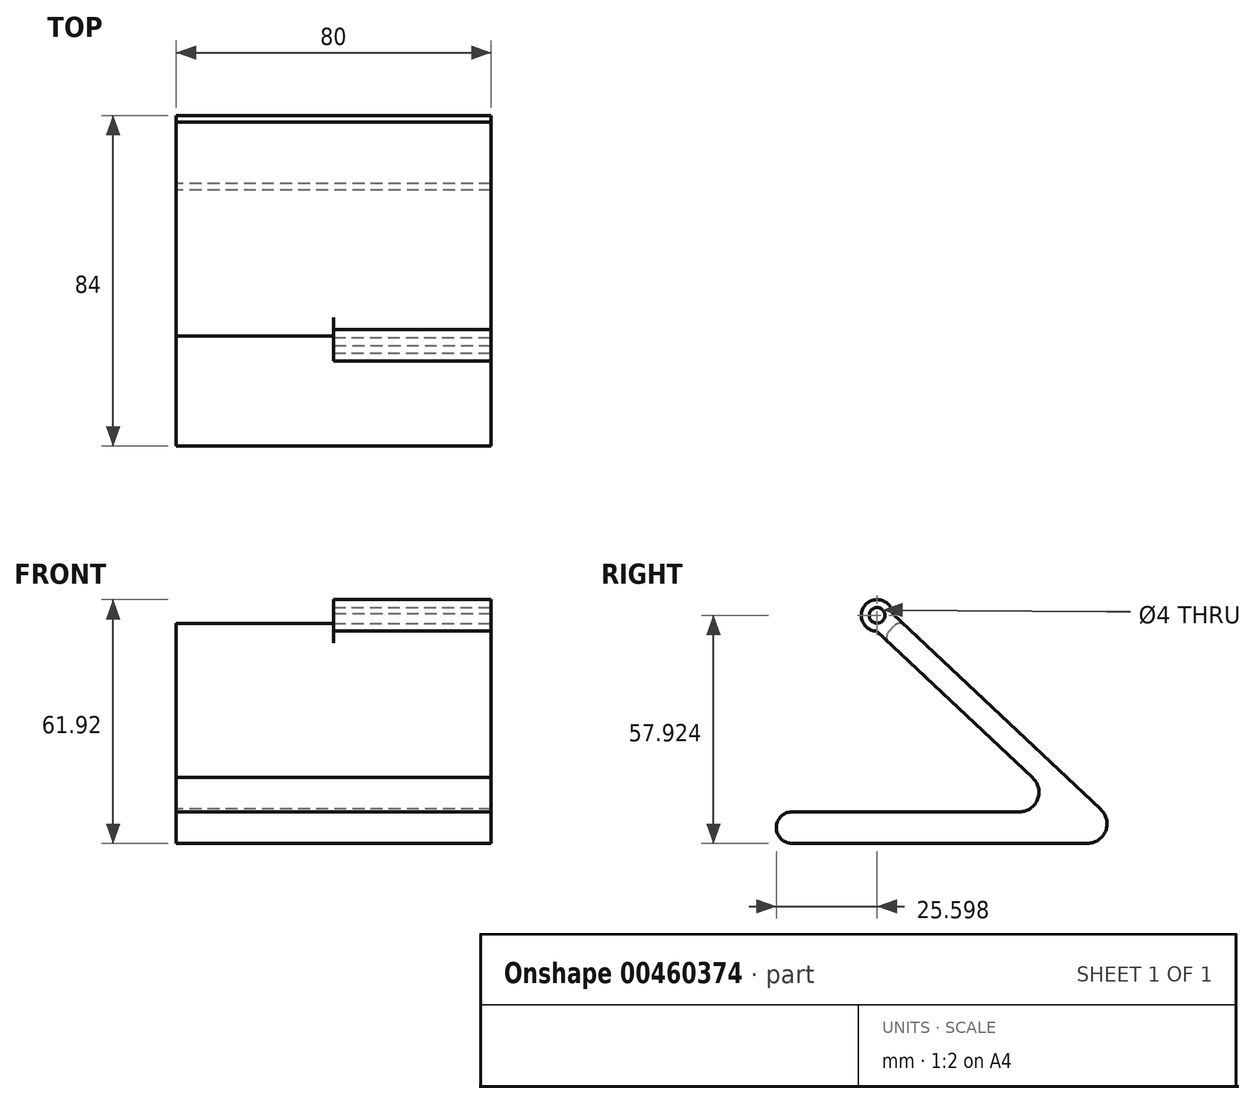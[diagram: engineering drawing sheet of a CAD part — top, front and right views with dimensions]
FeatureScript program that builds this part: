
annotation { "Feature Type Name" : "Feature", "Feature Type Description" : "" }
export const myFeature = defineFeature(function(context is Context, id is Id, definition is map)
    precondition{}
    {
        {
            var Q0;
            Q0=qCreatedBy(makeId("Right.planeOp"),FACE);
            var sketch = newSketch(context, id + "F0", { "sketchPlane" : qUnion([Q0])});
            skLineSegment(sketch, "E0", {"start": v(-63.48, -15.33) * mm, "end": v(11.52, -15.33) * mm});
            skLineSegment(sketch, "E1", {"start": v(-5.76, -7.33) * mm, "end": v(-63.48, -7.33) * mm});
            skPoint(sketch, "E2.visualSharp", {"position": v(7.24, -7.33) * mm});
            skArc(sketch, "E2.filletArc", {"start": v(-5.76, -7.33) * mm, "mid": v(-1.09, -4.13) * mm, "end": v(-2.4, 1.37) * mm});
            skPoint(sketch, "E3.visualSharp", {"position": v(24.5, -15.33) * mm});
            skArc(sketch, "E3.filletArc", {"start": v(11.52, -15.33) * mm, "mid": v(16.18, -12.13) * mm, "end": v(14.87, -6.63) * mm});
            skArc(sketch, "E4", {"start": v(-63.48, -7.33) * mm, "mid": v(-67.48, -11.33) * mm, "end": v(-63.48, -15.33) * mm});
            skLineSegment(sketch, "E5", {"start": v(-40.25, 36.94) * mm, "end": v(-36.23, 41.4) * mm});
            skLineSegment(sketch, "E6", {"start": v(-40.25, 36.94) * mm, "end": v(-2.4, 1.37) * mm});
            skLineSegment(sketch, "E7", {"start": v(-36.23, 41.4) * mm, "end": v(14.87, -6.63) * mm});
            skSolve(sketch);
        }
        {
            var Q0;
            Q0=makeQuery(id+"F0.imprint","IMPRINT",FACE,{"disambiguationData":[TD([[makeQuery(id+"F0.imprint","IMPRINT",EDGE,{"derivedFrom":sQuery(id+"F0.wireOp",EDGE,"E0")}),1.0]])]});
            extrude(context, id + "F1", {"entities" : qUnion([Q0]), "depth" : 40 * mm});
        }
        {
            var Q0;
            Q0=qCreatedBy(makeId("Right.planeOp"),FACE);
            cPlane(context, id + "F2", {"entities" : qUnion([Q0]), "cplaneType" : CPlaneType.OFFSET, "offset" : 40 * mm, "width" : 150 * mm, "height" : 150 * mm});
        }
        {
            var Q0;
            Q0=qCreatedBy(id+"F2.planeOp",FACE);
            var sketch = newSketch(context, id + "F3", { "sketchPlane" : qUnion([Q0])});
            skLineSegment(sketch, "E8.0.0", {"start": v(-36.23, 41.4) * mm, "end": v(-40.25, 36.94) * mm});
            skLineSegment(sketch, "E8.0.1", {"start": v(-40.25, 36.94) * mm, "end": v(-2.4, 1.37) * mm});
            skArc(sketch, "E8.0.2", {"start": v(-2.4, 1.37) * mm, "mid": v(-1.09, -4.13) * mm, "end": v(-5.76, -7.33) * mm});
            skLineSegment(sketch, "E8.0.3", {"start": v(-5.76, -7.33) * mm, "end": v(-63.48, -7.33) * mm});
            skArc(sketch, "E8.0.4", {"start": v(-63.48, -7.33) * mm, "mid": v(-67.48, -11.33) * mm, "end": v(-63.48, -15.33) * mm});
            skLineSegment(sketch, "E8.0.5", {"start": v(-63.48, -15.33) * mm, "end": v(11.52, -15.33) * mm});
            skArc(sketch, "E8.0.6", {"start": v(11.52, -15.33) * mm, "mid": v(16.18, -12.13) * mm, "end": v(14.87, -6.63) * mm});
            skLineSegment(sketch, "E8.0.7", {"start": v(14.87, -6.63) * mm, "end": v(-36.23, 41.4) * mm});
            skLineSegment(sketch, "E9", {"start": v(-40.25, 36.94) * mm, "end": v(-51.72, 47.72) * mm, "construction": true});
            skLineSegment(sketch, "E10", {"start": v(-36.23, 41.4) * mm, "end": v(-47.07, 51.59) * mm, "construction": true});
            skCircle(sketch, "E11", {"center": v(-41.88, 42.6) * mm, "radius": 4 * mm});
            skLineSegment(sketch, "E12", {"start": v(-42, 38.6) * mm, "end": v(-40.25, 36.94) * mm});
            skLineSegment(sketch, "E13", {"start": v(-37.9, 42.97) * mm, "end": v(-36.23, 41.4) * mm});
            skSolve(sketch);
        }
        {
            var Q0;
            Q0 = qSketchRegion(id + "F3", true);
            extrude(context, id + "F4", {"entities" : qUnion([Q0]), "operationType" : NewBodyOperationType.ADD, "depth" : 40 * mm});
        }
        {
            var Q0;
            Q0=qCreatedBy(id+"F2.planeOp",FACE);
            cPlane(context, id + "F5", {"entities" : qUnion([Q0]), "cplaneType" : CPlaneType.OFFSET, "offset" : 80 * mm, "width" : 150 * mm, "height" : 150 * mm});
        }
        {
            var Q0;
            Q0=qCreatedBy(id+"F5.planeOp",FACE);
            var sketch = newSketch(context, id + "F6", { "sketchPlane" : qUnion([Q0])});
            skLineSegment(sketch, "E14.0", {"start": v(-36.23, 41.4) * mm, "end": v(-40.25, 36.94) * mm});
            skLineSegment(sketch, "E14.1", {"start": v(-40.25, 36.94) * mm, "end": v(-2.4, 1.37) * mm});
            skArc(sketch, "E14.2", {"start": v(-2.4, 1.37) * mm, "mid": v(-1.09, -4.13) * mm, "end": v(-5.76, -7.33) * mm});
            skLineSegment(sketch, "E14.3", {"start": v(-5.76, -7.33) * mm, "end": v(-63.48, -7.33) * mm});
            skArc(sketch, "E14.4", {"start": v(-63.48, -7.33) * mm, "mid": v(-67.48, -11.33) * mm, "end": v(-63.48, -15.33) * mm});
            skLineSegment(sketch, "E14.5", {"start": v(-63.48, -15.33) * mm, "end": v(11.52, -15.33) * mm});
            skArc(sketch, "E14.6", {"start": v(11.52, -15.33) * mm, "mid": v(16.18, -12.13) * mm, "end": v(14.87, -6.63) * mm});
            skLineSegment(sketch, "E14.7", {"start": v(14.87, -6.63) * mm, "end": v(-36.23, 41.4) * mm});
            skLineSegment(sketch, "E14.8", {"start": v(-40.25, 36.94) * mm, "end": v(-51.72, 47.72) * mm});
            skLineSegment(sketch, "E14.9", {"start": v(-36.23, 41.4) * mm, "end": v(-47.07, 51.59) * mm});
            skCircle(sketch, "E14.10", {"center": v(-41.88, 42.6) * mm, "radius": 4 * mm});
            skLineSegment(sketch, "E14.11", {"start": v(-42, 38.6) * mm, "end": v(-40.25, 36.94) * mm});
            skLineSegment(sketch, "E14.12", {"start": v(-37.9, 42.97) * mm, "end": v(-36.23, 41.4) * mm});
            skPoint(sketch, "E14.13", {"position": v(-41.88, 42.6) * mm});
            skPoint(sketch, "E14.14", {"position": v(-41.88, 42.6) * mm});
            skArc(sketch, "E14.15.0", {"start": v(11.52, -15.33) * mm, "mid": v(16.18, -12.13) * mm, "end": v(14.87, -6.63) * mm});
            skLineSegment(sketch, "E14.15.1", {"start": v(14.87, -6.63) * mm, "end": v(-37.9, 42.97) * mm});
            skArc(sketch, "E14.15.2", {"start": v(-37.9, 42.97) * mm, "mid": v(-44.8, 45.33) * mm, "end": v(-42, 38.6) * mm});
            skLineSegment(sketch, "E14.15.3", {"start": v(-42, 38.6) * mm, "end": v(-2.4, 1.37) * mm});
            skArc(sketch, "E14.15.4", {"start": v(-2.4, 1.37) * mm, "mid": v(-1.09, -4.13) * mm, "end": v(-5.76, -7.33) * mm});
            skLineSegment(sketch, "E14.15.5", {"start": v(-5.76, -7.33) * mm, "end": v(-63.48, -7.33) * mm});
            skArc(sketch, "E14.15.6", {"start": v(-63.48, -7.33) * mm, "mid": v(-67.48, -11.33) * mm, "end": v(-63.48, -15.33) * mm});
            skLineSegment(sketch, "E14.15.7", {"start": v(-63.48, -15.33) * mm, "end": v(11.52, -15.33) * mm});
            skSolve(sketch);
        }
        {
            var Q0;
            Q0=sQuery(id+"F6.wireOp",VERTEX,"E14.13");
            var Q1;
            Q1=makeQuery(id+"F1.opExtrude","SWEPT_BODY",BODY,{"disambiguationData":[OSD([sQuery(id+"F0.wireOp",EDGE,"E0"),sQuery(id+"F0.wireOp",EDGE,"E1"),sQuery(id+"F0.wireOp",EDGE,"E2.filletArc"),sQuery(id+"F0.wireOp",EDGE,"E3.filletArc"),sQuery(id+"F0.wireOp",EDGE,"E4"),sQuery(id+"F0.wireOp",EDGE,"E5"),sQuery(id+"F0.wireOp",EDGE,"E6"),sQuery(id+"F0.wireOp",EDGE,"E7")])]});
            hole(context, id + "F7", {"style" : HoleStyle.SIMPLE, "endStyle" : HoleEndStyle.THROUGH, "holeDiameter" : 4 * mm, "isTappedThrough" : true, "tappedDepth" : 12 * mm, "tapClearance" : 3, "startFromSketch" : true, "locations" : qUnion([Q0]), "scope" : qUnion([Q1])});
        }
        {
            var Q0;
            Q0=makeQuery(id+"F1.opExtrude","SWEPT_EDGE",EDGE,{"disambiguationData":[OSD([sQuery(id+"F0.wireOp",EDGE,"E5"),sQuery(id+"F0.wireOp",EDGE,"E7")])]});
            var Q1;
            Q1=makeQuery(id+"F1.opExtrude","SWEPT_EDGE",EDGE,{"disambiguationData":[OSD([sQuery(id+"F0.wireOp",EDGE,"E5"),sQuery(id+"F0.wireOp",EDGE,"E6")])]});
            fillet(context, id + "F8", {"entities" : qUnion([Q0, Q1]), "radius" : 2 * mm, "allowEdgeOverflow" : false});
        }
    });
